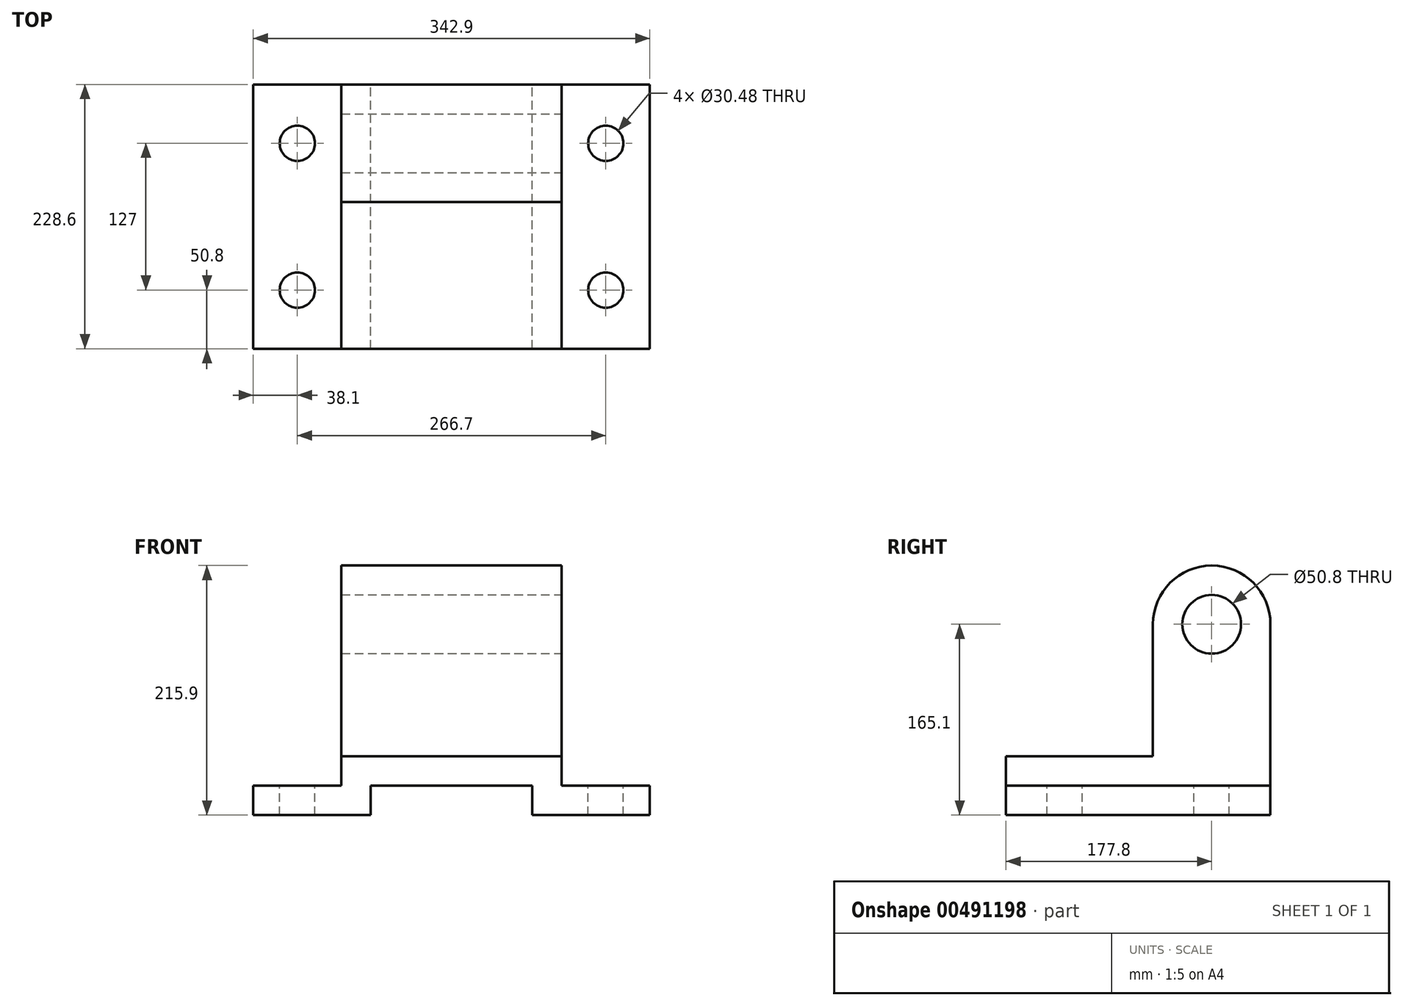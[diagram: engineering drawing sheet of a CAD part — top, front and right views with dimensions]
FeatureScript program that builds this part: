
annotation { "Feature Type Name" : "Feature", "Feature Type Description" : "" }
export const myFeature = defineFeature(function(context is Context, id is Id, definition is map)
    precondition{}
    {
        {
            var Q0;
            Q0=qCreatedBy(makeId("Front.planeOp"),FACE);
            var sketch = newSketch(context, id + "F0", { "sketchPlane" : qUnion([Q0])});
            skLineSegment(sketch, "E0", {"start": v(0, 25.4) * mm, "end": v(69.85, 25.4) * mm});
            skLineSegment(sketch, "E1", {"start": v(69.85, 25.4) * mm, "end": v(69.85, 0) * mm});
            skLineSegment(sketch, "E2", {"start": v(69.85, 0) * mm, "end": v(171.45, 0) * mm});
            skLineSegment(sketch, "E3", {"start": v(171.45, 0) * mm, "end": v(171.45, 25.4) * mm});
            skLineSegment(sketch, "E4", {"start": v(171.45, 25.4) * mm, "end": v(95.25, 25.4) * mm});
            skLineSegment(sketch, "E5", {"start": v(95.25, 25.4) * mm, "end": v(95.25, 50.8) * mm});
            skLineSegment(sketch, "E6", {"start": v(0, 50.8) * mm, "end": v(95.25, 50.8) * mm});
            skLineSegment(sketch, "E7.MirrorCS", {"start": v(-69.85, 25.4) * mm, "end": v(-69.85, 0) * mm});
            skLineSegment(sketch, "E8.MirrorCS", {"start": v(-171.45, 25.4) * mm, "end": v(-95.25, 25.4) * mm});
            skLineSegment(sketch, "E9.MirrorCS", {"start": v(-171.45, 0) * mm, "end": v(-171.45, 25.4) * mm});
            skLineSegment(sketch, "E10.MirrorCS", {"start": v(-69.85, 0) * mm, "end": v(-171.45, 0) * mm});
            skLineSegment(sketch, "E11.MirrorCS", {"start": v(0, 25.4) * mm, "end": v(-69.85, 25.4) * mm});
            skLineSegment(sketch, "E12.MirrorCS", {"start": v(0, 50.8) * mm, "end": v(-95.25, 50.8) * mm});
            skLineSegment(sketch, "E13.MirrorCS", {"start": v(-95.25, 25.4) * mm, "end": v(-95.25, 50.8) * mm});
            skSolve(sketch);
        }
        {
            var Q0;
            Q0=makeQuery(id+"F0.imprint","IMPRINT",FACE,{"disambiguationData":[TD([[makeQuery(id+"F0.imprint","IMPRINT",EDGE,{"derivedFrom":sQuery(id+"F0.wireOp",EDGE,"E0")}),1.0]])]});
            extrude(context, id + "F1", {"entities" : qUnion([Q0]), "depth" : 228.6 * mm});
        }
        {
            var Q0;
            Q0=makeQuery(id+"F1.opExtrude","SWEPT_FACE",FACE,{"disambiguationData":[OSD([sQuery(id+"F0.wireOp",EDGE,"E6"),sQuery(id+"F0.wireOp",EDGE,"E12.MirrorCS")])]});
            var sketch = newSketch(context, id + "F2", { "sketchPlane" : qUnion([Q0])});
            skLineSegment(sketch, "E14", {"start": v(-95.25, -228.6) * mm, "end": v(-95.25, -101.6) * mm});
            skLineSegment(sketch, "E15", {"start": v(-95.25, -101.6) * mm, "end": v(95.25, -101.6) * mm});
            skSolve(sketch);
        }
        {
            var Q0;
            {var subQ0=sQuery(id+"F2.wireOp",EDGE,"E15");Q0=makeQuery(id+"F2.imprint","IMPRINT",FACE,{"disambiguationData":[TD([[makeQuery(id+"F2.imprint","IMPRINT",EDGE,{"derivedFrom":subQ0}),1.0]])]});}
            extrude(context, id + "F3", {"entities" : qUnion([Q0]), "operationType" : NewBodyOperationType.ADD, "depth" : 114.3 * mm});
        }
        {
            var Q0;
            {var subQ0=sQuery(id+"F0.wireOp",EDGE,"E5");Q0=makeQuery(id+"F3.boolean.opBoolean","MERGE",FACE,{"derivedFrom":[makeQuery(id+"F1.opExtrude","SWEPT_FACE",FACE,{"disambiguationData":[OSD([subQ0])]}),makeQuery(id+"F3.opExtrude","SWEPT_FACE",FACE,{"disambiguationData":[OSD([subQ0,sQuery(id+"F0.wireOp",EDGE,"E6")])]})]});}
            var sketch = newSketch(context, id + "F4", { "sketchPlane" : qUnion([Q0])});
            skCircle(sketch, "E16", {"center": v(-50.8, 165.1) * mm, "radius": 50.8 * mm});
            skSolve(sketch);
        }
        {
            var Q0;
            {var subQ1=sQuery(id+"F0.wireOp",EDGE,"E6");var subQ2=sQuery(id+"F0.wireOp",EDGE,"E5");var subQ3=makeQuery(id+"F3.opExtrude","CAP_EDGE",EDGE,{"disambiguationData":[OSD([subQ2,subQ1])],"isStart":false});Q0=makeQuery(id+"F4.imprint","IMPRINT",FACE,{"disambiguationData":[TD([[makeQuery(id+"F4.imprint","IMPRINT",EDGE,{"derivedFrom":subQ3}),1.0]])]});}
            extrude(context, id + "F5", {"entities" : qUnion([Q0]), "operationType" : NewBodyOperationType.ADD, "oppositeDirection" : true, "depth" : 190.5 * mm});
        }
        {
            var Q0;
            {var subQ0=sQuery(id+"F0.wireOp",EDGE,"E13.MirrorCS");Q0=makeQuery(id+"F5.boolean.opBoolean","MERGE",FACE,{"derivedFrom":[makeQuery(id+"F3.boolean.opBoolean","MERGE",FACE,{"derivedFrom":[makeQuery(id+"F1.opExtrude","SWEPT_FACE",FACE,{"disambiguationData":[OSD([subQ0])]}),makeQuery(id+"F3.opExtrude","SWEPT_FACE",FACE,{"disambiguationData":[OSD([sQuery(id+"F0.wireOp",EDGE,"E12.MirrorCS"),subQ0])]})]}),makeQuery(id+"F5.opExtrude","CAP_FACE",FACE,{"disambiguationData":[OSD([sQuery(id+"F0.wireOp",EDGE,"E5"),sQuery(id+"F0.wireOp",EDGE,"E6"),sQuery(id+"F4.wireOp",EDGE,"E16")])],"isStart":false})]});}
            var sketch = newSketch(context, id + "F6", { "sketchPlane" : qUnion([Q0])});
            skSolve(sketch);
        }
        {
            var Q0;
            {var subQ0=sQuery(id+"F0.wireOp",EDGE,"E6");var subQ1=sQuery(id+"F0.wireOp",EDGE,"E5");Q0=makeQuery(id+"F5.boolean.opBoolean","MERGE",FACE,{"derivedFrom":[makeQuery(id+"F3.boolean.opBoolean","MERGE",FACE,{"derivedFrom":[makeQuery(id+"F1.opExtrude","SWEPT_FACE",FACE,{"disambiguationData":[OSD([subQ1])]}),makeQuery(id+"F3.opExtrude","SWEPT_FACE",FACE,{"disambiguationData":[OSD([subQ1,subQ0])]})]}),makeQuery(id+"F5.opExtrude","CAP_FACE",FACE,{"disambiguationData":[OSD([subQ1,subQ0,sQuery(id+"F4.wireOp",EDGE,"E16")])],"isStart":true})]});}
            var sketch = newSketch(context, id + "F7", { "sketchPlane" : qUnion([Q0])});
            skCircle(sketch, "E17", {"center": v(-50.8, 165.1) * mm, "radius": 25.4 * mm});
            skSolve(sketch);
        }
        {
            var Q0;
            Q0=sQuery(id+"F7.wireOp",VERTEX,"E17.center");
            var Q1;
            Q1=makeQuery(id+"F1.opExtrude","SWEPT_BODY",BODY,{"disambiguationData":[OSD([sQuery(id+"F0.wireOp",EDGE,"E0"),sQuery(id+"F0.wireOp",EDGE,"E1"),sQuery(id+"F0.wireOp",EDGE,"E2"),sQuery(id+"F0.wireOp",EDGE,"E3"),sQuery(id+"F0.wireOp",EDGE,"E4"),sQuery(id+"F0.wireOp",EDGE,"E5"),sQuery(id+"F0.wireOp",EDGE,"E6"),sQuery(id+"F0.wireOp",EDGE,"E7.MirrorCS"),sQuery(id+"F0.wireOp",EDGE,"E8.MirrorCS"),sQuery(id+"F0.wireOp",EDGE,"E9.MirrorCS"),sQuery(id+"F0.wireOp",EDGE,"E10.MirrorCS"),sQuery(id+"F0.wireOp",EDGE,"E11.MirrorCS"),sQuery(id+"F0.wireOp",EDGE,"E12.MirrorCS"),sQuery(id+"F0.wireOp",EDGE,"E13.MirrorCS")])]});
            hole(context, id + "F8", {"style" : HoleStyle.SIMPLE, "endStyle" : HoleEndStyle.THROUGH, "holeDiameter" : 50.8 * mm, "isTappedThrough" : true, "tappedDepth" : 12.7 * mm, "tapClearance" : 3, "locations" : qUnion([Q0]), "scope" : qUnion([Q1])});
        }
        {
            var Q0;
            Q0=makeQuery(id+"F1.opExtrude","SWEPT_FACE",FACE,{"disambiguationData":[OSD([sQuery(id+"F0.wireOp",EDGE,"E4")])]});
            var sketch = newSketch(context, id + "F9", { "sketchPlane" : qUnion([Q0])});
            skCircle(sketch, "E18", {"center": v(133.35, -50.8) * mm, "radius": 35.02 * mm});
            skCircle(sketch, "E19", {"center": v(133.35, -177.8) * mm, "radius": 29.18 * mm});
            skCircle(sketch, "E20", {"center": v(-133.35, -50.8) * mm, "radius": 26.57 * mm});
            skCircle(sketch, "E21", {"center": v(-133.35, -177.8) * mm, "radius": 26.96 * mm});
            skSolve(sketch);
        }
        {
            var Q0;
            Q0=sQuery(id+"F9.wireOp",VERTEX,"E20.center");
            var Q1;
            Q1=sQuery(id+"F9.wireOp",VERTEX,"E18.center");
            var Q2;
            Q2=sQuery(id+"F9.wireOp",VERTEX,"E21.center");
            var Q3;
            Q3=sQuery(id+"F9.wireOp",VERTEX,"E19.center");
            var Q4;
            Q4=makeQuery(id+"F1.opExtrude","SWEPT_BODY",BODY,{"disambiguationData":[OSD([sQuery(id+"F0.wireOp",EDGE,"E0"),sQuery(id+"F0.wireOp",EDGE,"E1"),sQuery(id+"F0.wireOp",EDGE,"E2"),sQuery(id+"F0.wireOp",EDGE,"E3"),sQuery(id+"F0.wireOp",EDGE,"E4"),sQuery(id+"F0.wireOp",EDGE,"E5"),sQuery(id+"F0.wireOp",EDGE,"E6"),sQuery(id+"F0.wireOp",EDGE,"E7.MirrorCS"),sQuery(id+"F0.wireOp",EDGE,"E8.MirrorCS"),sQuery(id+"F0.wireOp",EDGE,"E9.MirrorCS"),sQuery(id+"F0.wireOp",EDGE,"E10.MirrorCS"),sQuery(id+"F0.wireOp",EDGE,"E11.MirrorCS"),sQuery(id+"F0.wireOp",EDGE,"E12.MirrorCS"),sQuery(id+"F0.wireOp",EDGE,"E13.MirrorCS")])]});
            hole(context, id + "F10", {"style" : HoleStyle.SIMPLE, "endStyle" : HoleEndStyle.THROUGH, "holeDiameter" : 30.48 * mm, "isTappedThrough" : true, "tappedDepth" : 12.7 * mm, "tapClearance" : 3, "locations" : qUnion([Q0, Q1, Q2, Q3]), "scope" : qUnion([Q4])});
        }
    });
